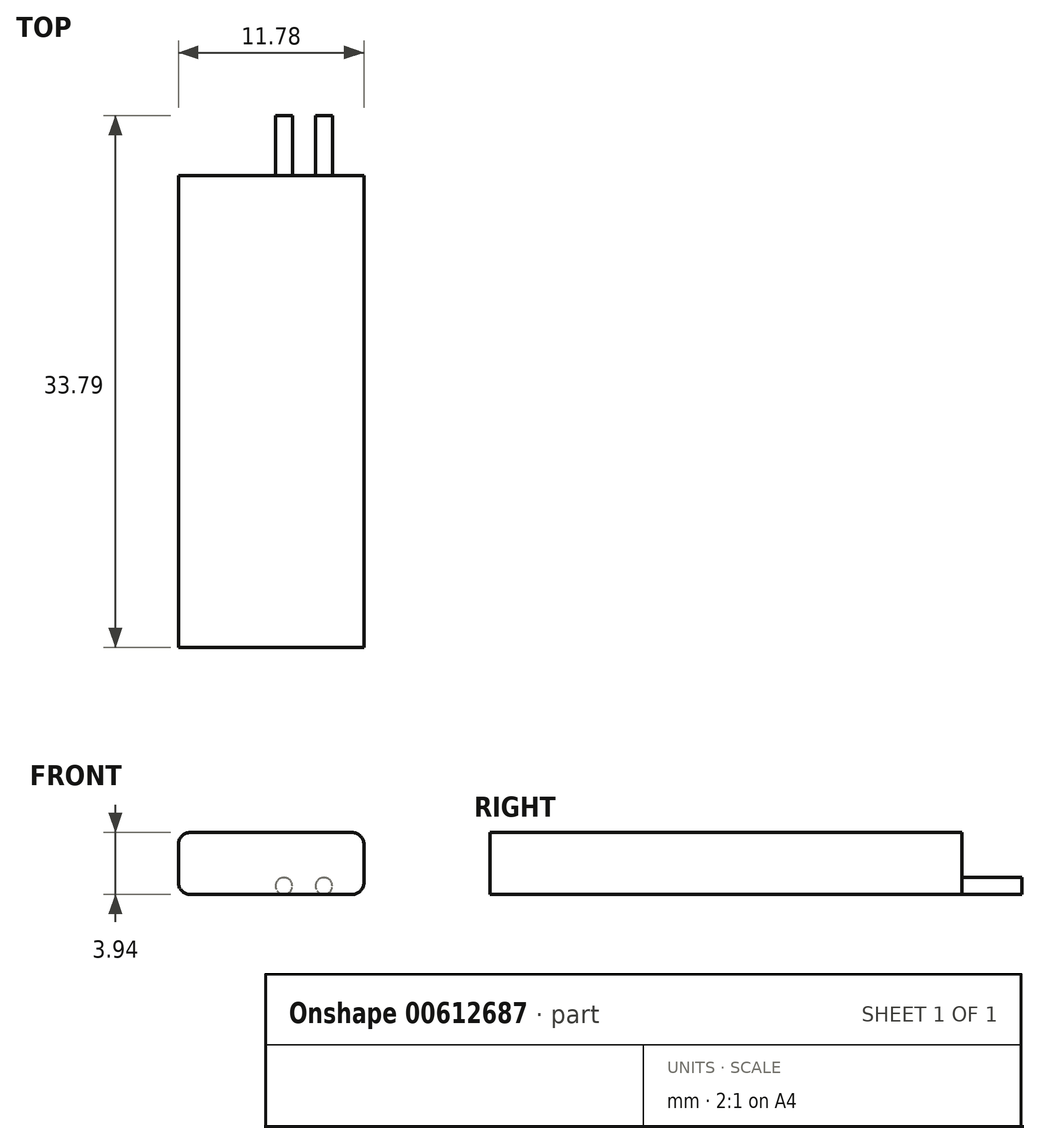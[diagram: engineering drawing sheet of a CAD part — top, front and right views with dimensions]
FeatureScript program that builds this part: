
annotation { "Feature Type Name" : "Feature", "Feature Type Description" : "" }
export const myFeature = defineFeature(function(context is Context, id is Id, definition is map)
    precondition{}
    {
        {
            var Q0;
            Q0=qCreatedBy(makeId("Top.planeOp"),FACE);
            var sketch = newSketch(context, id + "F0", { "sketchPlane" : qUnion([Q0])});
            skLineSegment(sketch, "E0.bottom", {"start": v(-5.9, 14.99) * mm, "end": v(5.9, 14.99) * mm});
            skLineSegment(sketch, "E0.top", {"start": v(-5.9, -14.99) * mm, "end": v(5.9, -14.99) * mm});
            skLineSegment(sketch, "E0.left", {"start": v(-5.9, 14.99) * mm, "end": v(-5.9, -14.99) * mm});
            skLineSegment(sketch, "E0.right", {"start": v(5.9, 14.99) * mm, "end": v(5.9, -14.99) * mm});
            skLineSegment(sketch, "E1", {"start": v(5.9, 14.99) * mm, "end": v(-5.9, -14.99) * mm, "construction": true});
            skSolve(sketch);
        }
        {
            var Q0;
            Q0 = qSketchRegion(id + "F0", true);
            extrude(context, id + "F1", {"entities" : qUnion([Q0]), "endBound" : BoundingType.SYMMETRIC, "depth" : 3.94 * mm, "offsetDistance" : 25.4 * mm});
        }
        {
            var Q0;
            Q0=makeQuery(id+"F1.opExtrude","CAP_EDGE",EDGE,{"disambiguationData":[OSD([sQuery(id+"F0.wireOp",EDGE,"E0.left")])],"isStart":false});
            var Q1;
            Q1=makeQuery(id+"F1.opExtrude","CAP_EDGE",EDGE,{"disambiguationData":[OSD([sQuery(id+"F0.wireOp",EDGE,"E0.left")])],"isStart":true});
            var Q2;
            Q2=makeQuery(id+"F1.opExtrude","CAP_EDGE",EDGE,{"disambiguationData":[OSD([sQuery(id+"F0.wireOp",EDGE,"E0.right")])],"isStart":true});
            var Q3;
            Q3=makeQuery(id+"F1.opExtrude","CAP_EDGE",EDGE,{"disambiguationData":[OSD([sQuery(id+"F0.wireOp",EDGE,"E0.right")])],"isStart":false});
            fillet(context, id + "F2", {"entities" : qUnion([Q0, Q1, Q2, Q3]), "radius" : 0.76 * mm, "tangentPropagation" : true, "allowEdgeOverflow" : false});
        }
        {
            var Q0;
            Q0=makeQuery(id+"F1.opExtrude","SWEPT_FACE",FACE,{"disambiguationData":[OSD([sQuery(id+"F0.wireOp",EDGE,"E0.bottom")])]});
            var sketch = newSketch(context, id + "F3", { "sketchPlane" : qUnion([Q0])});
            skCircle(sketch, "E2", {"center": v(-3.35, -1.44) * mm, "radius": 0.53 * mm});
            skCircle(sketch, "E3.1.0.0", {"center": v(-0.81, -1.44) * mm, "radius": 0.53 * mm});
            skLineSegment(sketch, "E3.direction1", {"start": v(-3.35, -1.44) * mm, "end": v(-0.81, -1.44) * mm, "construction": true});
            skSolve(sketch);
        }
        {
            var Q0;
            Q0 = qSketchRegion(id + "F3", true);
            extrude(context, id + "F4", {"entities" : qUnion([Q0]), "operationType" : NewBodyOperationType.ADD, "depth" : 3.8 * mm, "offsetDistance" : 25.4 * mm});
        }
    });
